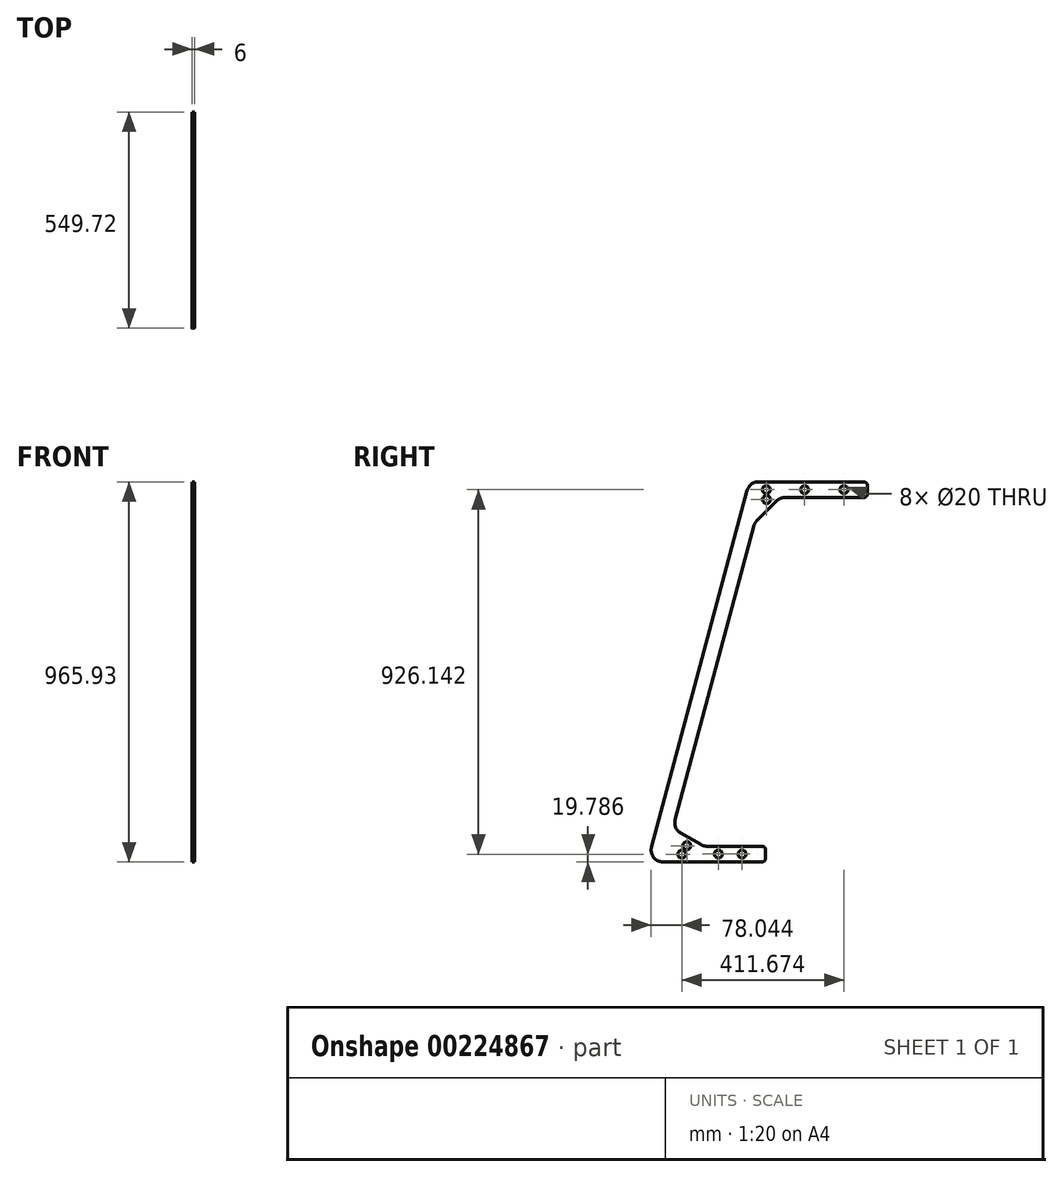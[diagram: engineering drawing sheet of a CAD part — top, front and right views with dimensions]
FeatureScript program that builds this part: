
annotation { "Feature Type Name" : "Feature", "Feature Type Description" : "" }
export const myFeature = defineFeature(function(context is Context, id is Id, definition is map)
    precondition{}
    {
        {
            var Q0;
            Q0=qCreatedBy(makeId("Right.planeOp"),FACE);
            var sketch = newSketch(context, id + "F0", { "sketchPlane" : qUnion([Q0])});
            skLineSegment(sketch, "E0", {"start": v(196.3, -329.45) * mm, "end": v(-54.6, -329.45) * mm});
            skLineSegment(sketch, "E1", {"start": v(-83.58, -291.68) * mm, "end": v(159.16, 614.24) * mm});
            skLineSegment(sketch, "E2", {"start": v(188.14, 636.48) * mm, "end": v(455.12, 636.48) * mm});
            skLineSegment(sketch, "E3", {"start": v(465.12, 626.48) * mm, "end": v(465.12, 606.48) * mm});
            skLineSegment(sketch, "E4", {"start": v(206.3, -299.45) * mm, "end": v(206.3, -319.45) * mm});
            skLineSegment(sketch, "E5", {"start": v(455.12, 596.48) * mm, "end": v(254.83, 596.48) * mm});
            skLineSegment(sketch, "E6", {"start": v(233.61, 587.7) * mm, "end": v(184.44, 538.52) * mm});
            skLineSegment(sketch, "E7", {"start": v(176.68, 525.07) * mm, "end": v(-23.56, -222.21) * mm});
            skLineSegment(sketch, "E8", {"start": v(-9.58, -255.96) * mm, "end": v(41.47, -285.43) * mm});
            skLineSegment(sketch, "E9", {"start": v(56.47, -289.45) * mm, "end": v(196.3, -289.45) * mm});
            skPoint(sketch, "E10.visualSharp", {"position": v(165.12, 636.48) * mm});
            skArc(sketch, "E10.filletArc", {"start": v(188.14, 636.48) * mm, "mid": v(169.88, 630.28) * mm, "end": v(159.16, 614.24) * mm});
            skPoint(sketch, "E11.visualSharp", {"position": v(465.12, 636.48) * mm});
            skArc(sketch, "E11.filletArc", {"start": v(465.12, 626.48) * mm, "mid": v(462.19, 633.55) * mm, "end": v(455.12, 636.48) * mm});
            skPoint(sketch, "E12.visualSharp", {"position": v(465.12, 596.48) * mm});
            skArc(sketch, "E12.filletArc", {"start": v(455.12, 596.48) * mm, "mid": v(462.19, 599.4) * mm, "end": v(465.12, 606.48) * mm});
            skPoint(sketch, "E13.visualSharp", {"position": v(-29.51, -244.45) * mm});
            skArc(sketch, "E13.filletArc", {"start": v(-23.56, -222.21) * mm, "mid": v(-22.3, -241.46) * mm, "end": v(-9.58, -255.96) * mm});
            skPoint(sketch, "E14.visualSharp", {"position": v(48.43, -289.45) * mm});
            skArc(sketch, "E14.filletArc", {"start": v(41.47, -285.43) * mm, "mid": v(48.7, -288.42) * mm, "end": v(56.47, -289.45) * mm});
            skPoint(sketch, "E15.visualSharp", {"position": v(178.76, 532.84) * mm});
            skArc(sketch, "E15.filletArc", {"start": v(184.44, 538.52) * mm, "mid": v(179.68, 532.3) * mm, "end": v(176.68, 525.07) * mm});
            skPoint(sketch, "E16.visualSharp", {"position": v(242.4, 596.48) * mm});
            skArc(sketch, "E16.filletArc", {"start": v(254.83, 596.48) * mm, "mid": v(243.34, 594.2) * mm, "end": v(233.61, 587.7) * mm});
            skPoint(sketch, "E17.visualSharp", {"position": v(-93.7, -329.45) * mm});
            skArc(sketch, "E17.filletArc", {"start": v(-83.58, -291.68) * mm, "mid": v(-78.4, -317.7) * mm, "end": v(-54.6, -329.45) * mm});
            skPoint(sketch, "E18.visualSharp", {"position": v(206.3, -289.45) * mm});
            skArc(sketch, "E18.filletArc", {"start": v(206.3, -299.45) * mm, "mid": v(203.37, -292.38) * mm, "end": v(196.3, -289.45) * mm});
            skPoint(sketch, "E19.visualSharp", {"position": v(206.3, -329.45) * mm});
            skArc(sketch, "E19.filletArc", {"start": v(196.3, -329.45) * mm, "mid": v(203.37, -326.52) * mm, "end": v(206.3, -319.45) * mm});
            skSolve(sketch);
        }
        {
            var Q0;
            Q0=makeQuery(id+"F0.imprint","IMPRINT",FACE,{"disambiguationData":[TD([[makeQuery(id+"F0.imprint","IMPRINT",EDGE,{"derivedFrom":sQuery(id+"F0.wireOp",EDGE,"E0")}),-1.0]])]});
            var sketch = newSketch(context, id + "F1", { "sketchPlane" : qUnion([Q0])});
            skLineSegment(sketch, "E20", {"start": v(449.53, 616.48) * mm, "end": v(218.92, 616.48) * mm, "construction": true});
            skCircle(sketch, "E21", {"center": v(405.12, 616.48) * mm, "radius": 10 * mm});
            skCircle(sketch, "E22", {"center": v(305.12, 616.48) * mm, "radius": 10 * mm});
            skLineSegment(sketch, "E23", {"start": v(270.1, -309.45) * mm, "end": v(89.34, -309.45) * mm, "construction": true});
            skCircle(sketch, "E24", {"center": v(146.3, -309.45) * mm, "radius": 10 * mm});
            skCircle(sketch, "E25", {"center": v(86.3, -309.45) * mm, "radius": 10 * mm});
            skSolve(sketch);
        }
        {
            var Q0;
            Q0 = qSketchRegion(id + "F0", true);
            extrude(context, id + "F2", {"entities" : qUnion([Q0]), "oppositeDirection" : true, "depth" : 6 * mm});
        }
        {
            var Q0;
            Q0 = qSketchRegion(id + "F1", true);
            extrude(context, id + "F3", {"entities" : qUnion([Q0]), "operationType" : NewBodyOperationType.REMOVE, "endBound" : BoundingType.THROUGH_ALL, "oppositeDirection" : true, "depth" : 25 * mm});
        }
        {
            var Q0;
            Q0=makeQuery(id+"F2.opExtrude","CAP_FACE",FACE,{"disambiguationData":[OSD([sQuery(id+"F0.wireOp",EDGE,"E0"),sQuery(id+"F0.wireOp",EDGE,"E1"),sQuery(id+"F0.wireOp",EDGE,"E2"),sQuery(id+"F0.wireOp",EDGE,"E3"),sQuery(id+"F0.wireOp",EDGE,"E4"),sQuery(id+"F0.wireOp",EDGE,"E5"),sQuery(id+"F0.wireOp",EDGE,"E6"),sQuery(id+"F0.wireOp",EDGE,"E7"),sQuery(id+"F0.wireOp",EDGE,"E8"),sQuery(id+"F0.wireOp",EDGE,"E9"),sQuery(id+"F0.wireOp",EDGE,"E10.filletArc"),sQuery(id+"F0.wireOp",EDGE,"E11.filletArc"),sQuery(id+"F0.wireOp",EDGE,"E12.filletArc"),sQuery(id+"F0.wireOp",EDGE,"E13.filletArc"),sQuery(id+"F0.wireOp",EDGE,"E14.filletArc"),sQuery(id+"F0.wireOp",EDGE,"E15.filletArc"),sQuery(id+"F0.wireOp",EDGE,"E16.filletArc"),sQuery(id+"F0.wireOp",EDGE,"E17.filletArc"),sQuery(id+"F0.wireOp",EDGE,"E18.filletArc"),sQuery(id+"F0.wireOp",EDGE,"E19.filletArc")])],"isStart":true});
            var sketch = newSketch(context, id + "F4", { "sketchPlane" : qUnion([Q0])});
            skLineSegment(sketch, "E26", {"start": v(209.03, 563.1) * mm, "end": v(141.32, 630.82) * mm, "construction": true});
            skLineSegment(sketch, "E27", {"start": v(131.36, 510.47) * mm, "end": v(170, 500.12) * mm, "construction": true});
            skCircle(sketch, "E28", {"center": v(208.14, 616.48) * mm, "radius": 10 * mm});
            skLineSegment(sketch, "E29", {"start": v(208.14, 616.48) * mm, "end": v(208.46, 591.48) * mm, "construction": true});
            skCircle(sketch, "E30", {"center": v(208.46, 591.48) * mm, "radius": 10 * mm});
            skLineSegment(sketch, "E31", {"start": v(188.14, 636.48) * mm, "end": v(188.14, 665.44) * mm, "construction": true});
            skLineSegment(sketch, "E32", {"start": v(86.3, -309.45) * mm, "end": v(32.78, -309.45) * mm, "construction": true});
            skLineSegment(sketch, "E33", {"start": v(-54.6, -329.45) * mm, "end": v(-54.6, -259.19) * mm, "construction": true});
            skLineSegment(sketch, "E34", {"start": v(15.94, -270.7) * mm, "end": v(-56.92, -396.9) * mm, "construction": true});
            skCircle(sketch, "E35", {"center": v(5.94, -288.01) * mm, "radius": 10 * mm});
            skCircle(sketch, "E36", {"center": v(-6.56, -309.66) * mm, "radius": 10 * mm});
            skSolve(sketch);
        }
        {
            var Q0;
            Q0 = qSketchRegion(id + "F4", true);
            extrude(context, id + "F5", {"entities" : qUnion([Q0]), "operationType" : NewBodyOperationType.REMOVE, "endBound" : BoundingType.THROUGH_ALL, "oppositeDirection" : true, "depth" : 25 * mm});
        }
    });
